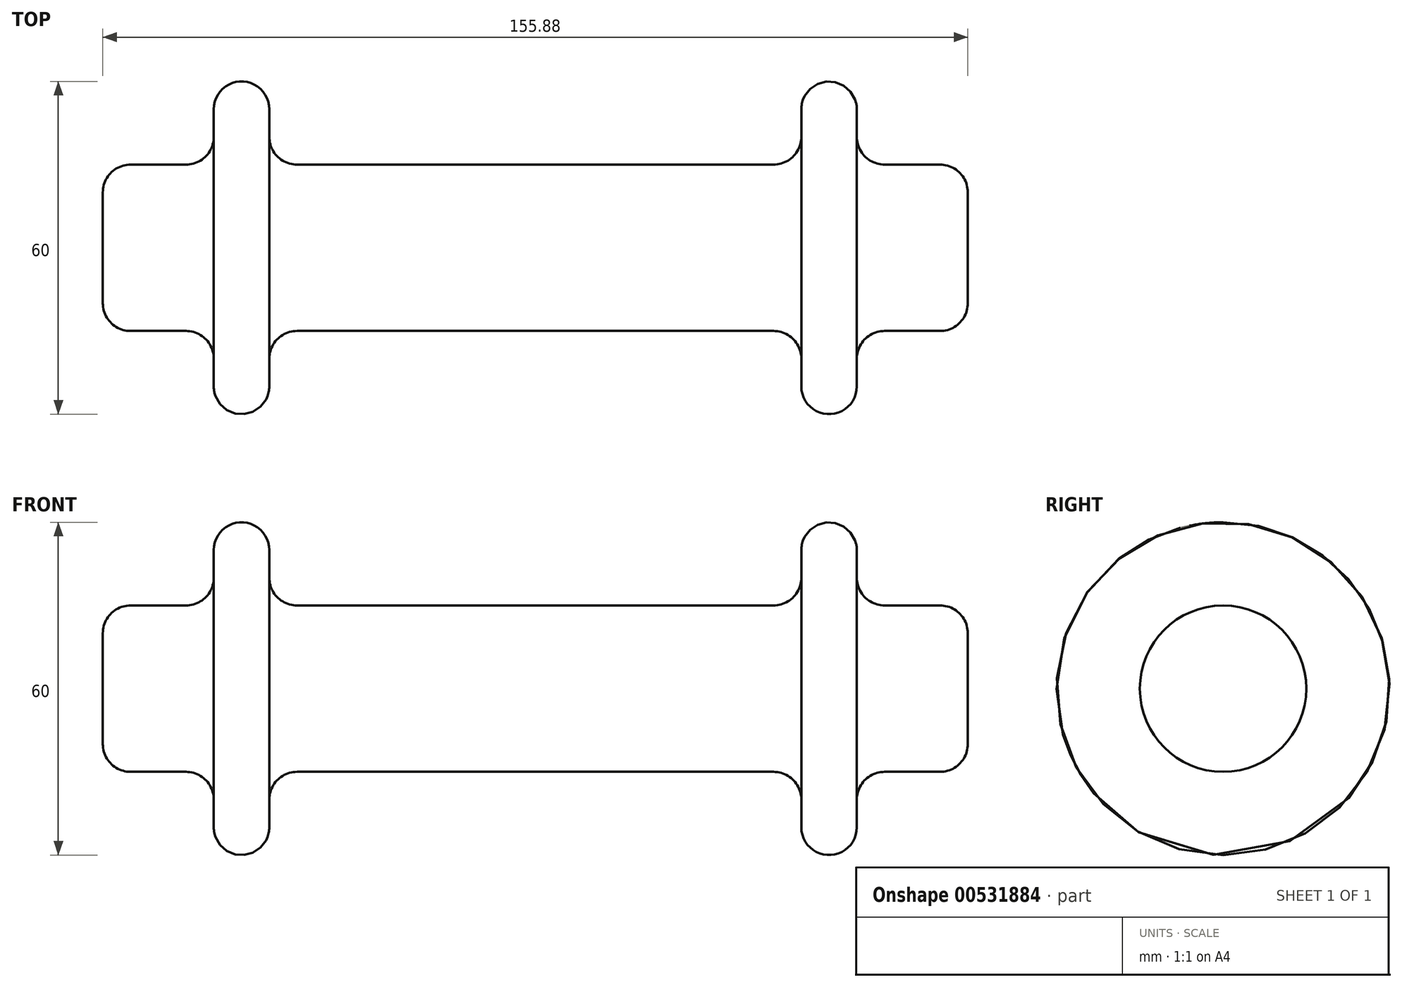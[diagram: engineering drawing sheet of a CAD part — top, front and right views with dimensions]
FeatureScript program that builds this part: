
annotation { "Feature Type Name" : "Feature", "Feature Type Description" : "" }
export const myFeature = defineFeature(function(context is Context, id is Id, definition is map)
    precondition{}
    {
        {
            var Q0;
            Q0=qCreatedBy(makeId("Front.planeOp"),FACE);
            var sketch = newSketch(context, id + "F0", { "sketchPlane" : qUnion([Q0])});
            skLineSegment(sketch, "E0", {"start": v(0, 0) * mm, "end": v(0, 15) * mm});
            skLineSegment(sketch, "E1", {"start": v(0, 15) * mm, "end": v(42.94, 15) * mm});
            skLineSegment(sketch, "E2", {"start": v(47.94, 20) * mm, "end": v(47.94, 30) * mm});
            skLineSegment(sketch, "E3", {"start": v(47.94, 30) * mm, "end": v(57.94, 30) * mm});
            skLineSegment(sketch, "E4", {"start": v(57.94, 30) * mm, "end": v(57.94, 15) * mm});
            skLineSegment(sketch, "E5", {"start": v(57.94, 15) * mm, "end": v(77.94, 15) * mm});
            skLineSegment(sketch, "E6", {"start": v(77.94, 15) * mm, "end": v(77.94, 0) * mm});
            skLineSegment(sketch, "E7", {"start": v(77.94, 0) * mm, "end": v(0, 0) * mm});
            skPoint(sketch, "E8.visualSharp", {"position": v(47.94, 15) * mm});
            skArc(sketch, "E8.filletArc", {"start": v(42.94, 15) * mm, "mid": v(46.47, 16.46) * mm, "end": v(47.94, 20) * mm});
            skSolve(sketch);
        }
        {
            var Q0;
            Q0=makeQuery(id+"F0.imprint","IMPRINT",FACE,{"disambiguationData":[TD([[makeQuery(id+"F0.imprint","IMPRINT",EDGE,{"derivedFrom":sQuery(id+"F0.wireOp",EDGE,"E0")}),-1.0]])]});
            var Q1;
            Q1=sQuery(id+"F0.wireOp",EDGE,"E7");
            revolve(context, id + "F1", {"entities" : qUnion([Q0]), "axis" : qUnion([Q1]), "revolveType" : RevolveType.FULL});
        }
        {
            var Q0;
            Q0=makeQuery(id+"F1.opRevolve","SWEPT_BODY",BODY,{"disambiguationData":[OSD([sQuery(id+"F0.wireOp",EDGE,"E0"),sQuery(id+"F0.wireOp",EDGE,"E1"),sQuery(id+"F0.wireOp",EDGE,"E2"),sQuery(id+"F0.wireOp",EDGE,"E3"),sQuery(id+"F0.wireOp",EDGE,"E4"),sQuery(id+"F0.wireOp",EDGE,"E5"),sQuery(id+"F0.wireOp",EDGE,"E6"),sQuery(id+"F0.wireOp",EDGE,"E7")])]});
            var Q1;
            Q1=qCreatedBy(makeId("Right.planeOp"),FACE);
            mirror(context, id + "F2", {"operationType" : NewBodyOperationType.ADD, "entities" : qUnion([Q0]), "mirrorPlane" : qUnion([Q1])});
        }
        {
            var Q0;
            Q0=makeQuery(id+"F2.opPattern","COPY",FACE,{"derivedFrom":makeQuery(id+"F1.opRevolve","SWEPT_FACE",FACE,{"disambiguationData":[OSD([sQuery(id+"F0.wireOp",EDGE,"E3")])]}),"instanceName":"1"});
            var Q1;
            Q1=makeQuery(id+"F1.opRevolve","SWEPT_FACE",FACE,{"disambiguationData":[OSD([sQuery(id+"F0.wireOp",EDGE,"E3")])]});
            fillet(context, id + "F3", {"entities" : qUnion([Q0, Q1]), "radius" : 5 * mm, "tangentPropagation" : true, "allowEdgeOverflow" : false});
        }
        {
            var Q0;
            Q0=makeQuery(id+"F1.opRevolve","SWEPT_FACE",FACE,{"disambiguationData":[OSD([sQuery(id+"F0.wireOp",EDGE,"E6")])]});
            var Q1;
            Q1=makeQuery(id+"F1.opRevolve","SWEPT_FACE",FACE,{"disambiguationData":[OSD([sQuery(id+"F0.wireOp",EDGE,"E5")])]});
            var Q2;
            Q2=makeQuery(id+"F2.opPattern","COPY",FACE,{"derivedFrom":makeQuery(id+"F1.opRevolve","SWEPT_FACE",FACE,{"disambiguationData":[OSD([sQuery(id+"F0.wireOp",EDGE,"E5")])]}),"instanceName":"1"});
            fillet(context, id + "F4", {"entities" : qUnion([Q0, Q1, Q2]), "radius" : 5 * mm, "tangentPropagation" : true, "allowEdgeOverflow" : false});
        }
    });
